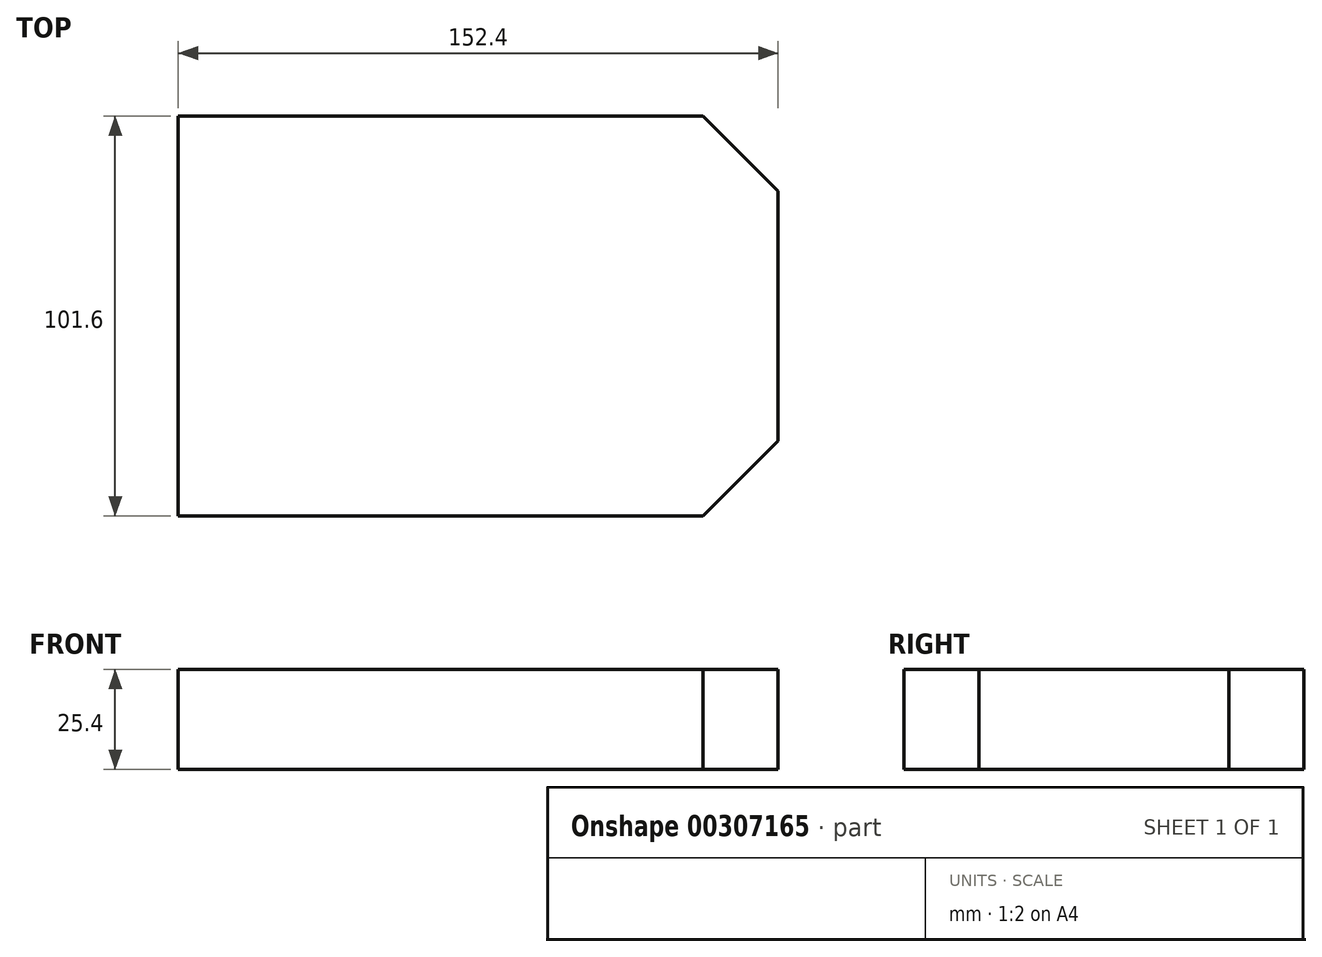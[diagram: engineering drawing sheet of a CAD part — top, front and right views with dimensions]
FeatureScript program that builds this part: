
annotation { "Feature Type Name" : "Feature", "Feature Type Description" : "" }
export const myFeature = defineFeature(function(context is Context, id is Id, definition is map)
    precondition{}
    {
        {
            var Q0;
            Q0=qCreatedBy(makeId("Top.planeOp"),FACE);
            var sketch = newSketch(context, id + "F0", { "sketchPlane" : qUnion([Q0])});
            skLineSegment(sketch, "E0", {"start": v(-76.67, 45.11) * mm, "end": v(-76.67, -56.49) * mm});
            skLineSegment(sketch, "E1", {"start": v(56.68, -56.49) * mm, "end": v(75.73, -37.44) * mm});
            skLineSegment(sketch, "E2", {"start": v(56.68, 45.11) * mm, "end": v(75.73, 26.06) * mm});
            skLineSegment(sketch, "E3", {"start": v(75.73, 26.06) * mm, "end": v(75.73, -37.44) * mm});
            skLineSegment(sketch, "E4", {"start": v(56.68, 45.11) * mm, "end": v(-76.67, 45.11) * mm});
            skLineSegment(sketch, "E5", {"start": v(-76.67, -56.49) * mm, "end": v(56.68, -56.49) * mm});
            skSolve(sketch);
        }
        {
            var Q0;
            Q0=makeQuery(id+"F0.imprint","IMPRINT",FACE,{"disambiguationData":[TD([[makeQuery(id+"F0.imprint","IMPRINT",EDGE,{"derivedFrom":sQuery(id+"F0.wireOp",EDGE,"E0")}),1.0]])]});
            extrude(context, id + "F1", {"entities" : qUnion([Q0]), "depth" : 25.4 * mm});
        }
    });
